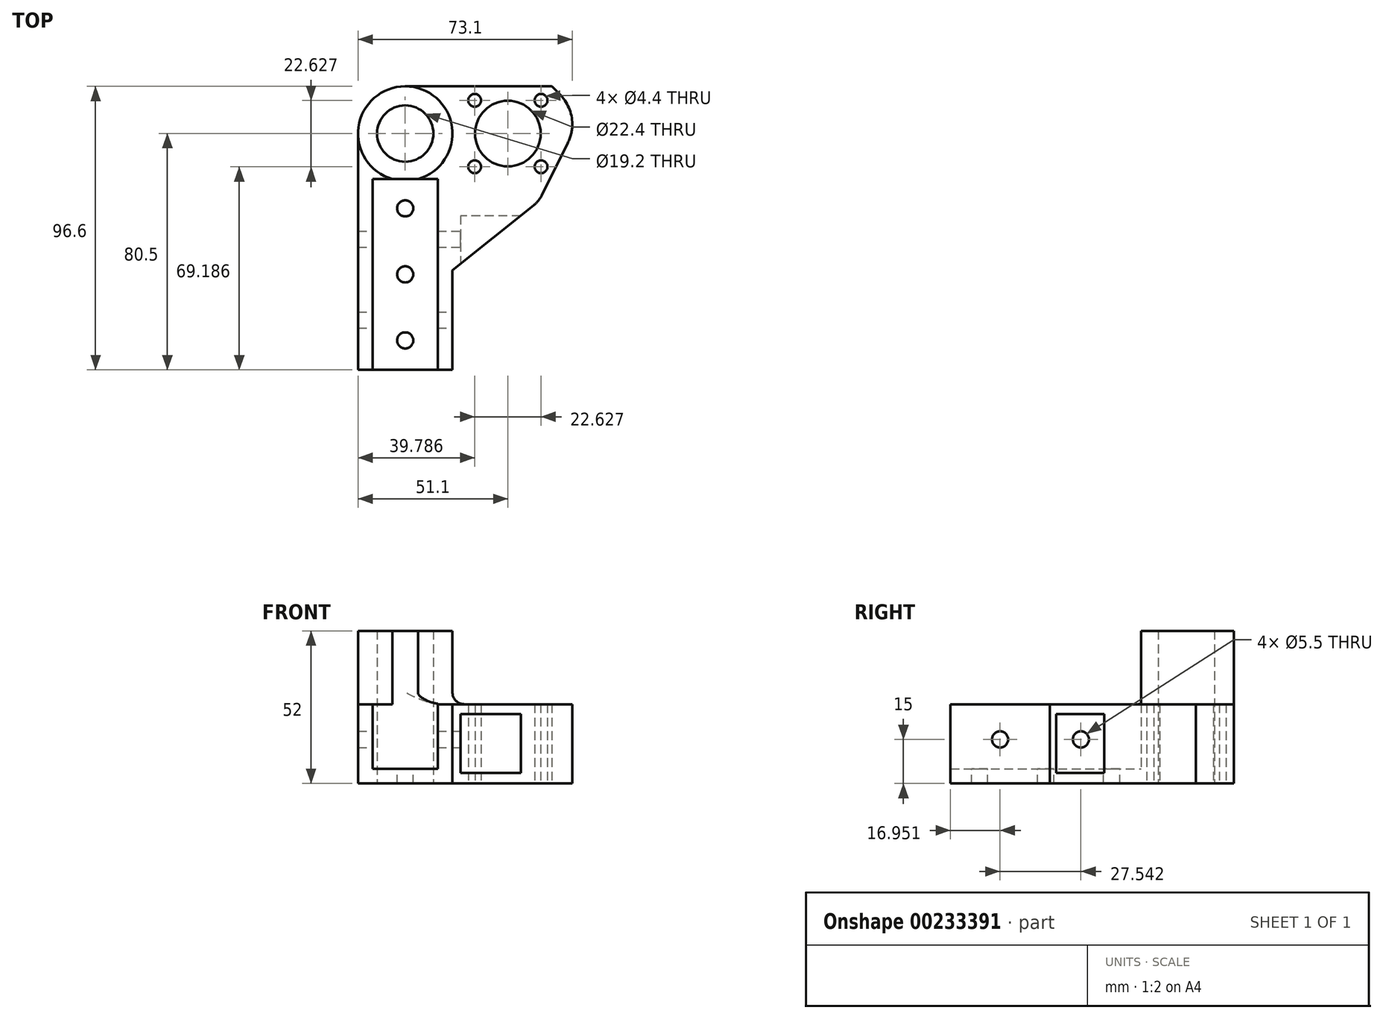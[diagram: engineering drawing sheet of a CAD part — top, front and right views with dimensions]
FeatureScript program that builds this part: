
annotation { "Feature Type Name" : "Feature", "Feature Type Description" : "" }
export const myFeature = defineFeature(function(context is Context, id is Id, definition is map)
    precondition{}
    {
        {
            var Q0;
            Q0=qCreatedBy(makeId("Top.planeOp"),FACE);
            var sketch = newSketch(context, id + "F0", { "sketchPlane" : qUnion([Q0])});
            skLineSegment(sketch, "E0.bottom", {"start": v(-10.1, -32.5) * mm, "end": v(10.1, -32.5) * mm, "construction": true});
            skLineSegment(sketch, "E0.top", {"start": v(-10.1, 32.5) * mm, "end": v(10.1, 32.5) * mm, "construction": true});
            skLineSegment(sketch, "E0.left", {"start": v(-10.1, -32.5) * mm, "end": v(-10.1, 32.5) * mm, "construction": true});
            skLineSegment(sketch, "E0.right", {"start": v(10.1, -32.5) * mm, "end": v(10.1, 32.5) * mm, "construction": true});
            skPoint(sketch, "E0.middle", {"position": v(0, 0) * mm});
            skLineSegment(sketch, "E1.bottom", {"start": v(-16.1, -32.5) * mm, "end": v(16.1, -32.5) * mm});
            skLineSegment(sketch, "E1.top", {"start": v(-16.1, 32.5) * mm, "end": v(16.1, 32.5) * mm});
            skLineSegment(sketch, "E1.left", {"start": v(-16.1, -32.5) * mm, "end": v(-16.1, 32.5) * mm});
            skLineSegment(sketch, "E1.right", {"start": v(16.1, -32.5) * mm, "end": v(16.1, 32.5) * mm});
            skCircle(sketch, "E2", {"center": v(0, 48) * mm, "radius": 9.6 * mm});
            skLineSegment(sketch, "E3", {"start": v(-16.1, 32.5) * mm, "end": v(-16.1, 48) * mm});
            skLineSegment(sketch, "E4", {"start": v(16.1, 32.5) * mm, "end": v(16.1, 48) * mm});
            skArc(sketch, "E5", {"start": v(16.1, 48) * mm, "mid": v(0, 64.1) * mm, "end": v(-16.1, 48) * mm});
            skCircle(sketch, "E6", {"center": v(35, 48) * mm, "radius": 11.2 * mm});
            skLineSegment(sketch, "E7", {"start": v(35, 48) * mm, "end": v(57, 48) * mm, "construction": true});
            skLineSegment(sketch, "E8", {"start": v(0, 64.1) * mm, "end": v(57, 64.1) * mm});
            skLineSegment(sketch, "E9", {"start": v(57, 64.1) * mm, "end": v(57, 48) * mm});
            skLineSegment(sketch, "E10", {"start": v(57, 48) * mm, "end": v(46.51, 26.9) * mm});
            skLineSegment(sketch, "E11", {"start": v(43.8, 23.53) * mm, "end": v(16.1, 1.4) * mm});
            skCircle(sketch, "E12", {"center": v(35, 48) * mm, "radius": 16 * mm, "construction": true});
            skLineSegment(sketch, "E13", {"start": v(35, 48) * mm, "end": v(46.31, 59.31) * mm, "construction": true});
            skCircle(sketch, "E14", {"center": v(46.31, 59.31) * mm, "radius": 2.2 * mm});
            skCircle(sketch, "E15.1.0", {"center": v(23.69, 59.31) * mm, "radius": 2.2 * mm});
            skCircle(sketch, "E15.2.0", {"center": v(23.69, 36.69) * mm, "radius": 2.2 * mm});
            skCircle(sketch, "E15.3.0", {"center": v(46.31, 36.69) * mm, "radius": 2.2 * mm});
            skPoint(sketch, "E16.visualSharp", {"position": v(45.53, 24.91) * mm});
            skArc(sketch, "E16.filletArc", {"start": v(43.8, 23.53) * mm, "mid": v(45.34, 25.06) * mm, "end": v(46.51, 26.9) * mm});
            skSolve(sketch);
        }
        {
            var Q0;
            Q0 = qSketchRegion(id + "F0", true);
            var Q1;
            {var subQ1=sQuery(id+"F0.wireOp",EDGE,"E1.bottom");Q1=makeQuery(id+"F0.imprint","IMPRINT",FACE,{"disambiguationData":[TD([[makeQuery(id+"F0.imprint","IMPRINT",EDGE,{"derivedFrom":subQ1}),1.0]])]});}
            extrude(context, id + "F1", {"entities" : qUnion([Q0, Q1]), "depth" : 5 * mm});
        }
        {
            var Q0;
            Q0=makeQuery(id+"F1.opExtrude","CAP_FACE",FACE,{"disambiguationData":[OSD([sQuery(id+"F0.wireOp",EDGE,"E1.bottom"),sQuery(id+"F0.wireOp",EDGE,"E1.left"),sQuery(id+"F0.wireOp",EDGE,"E1.right"),sQuery(id+"F0.wireOp",EDGE,"E2"),sQuery(id+"F0.wireOp",EDGE,"E3"),sQuery(id+"F0.wireOp",EDGE,"E5"),sQuery(id+"F0.wireOp",EDGE,"E6"),sQuery(id+"F0.wireOp",EDGE,"E8"),sQuery(id+"F0.wireOp",EDGE,"E9"),sQuery(id+"F0.wireOp",EDGE,"E10"),sQuery(id+"F0.wireOp",EDGE,"E11")])],"isStart":false});
            var sketch = newSketch(context, id + "F2", { "sketchPlane" : qUnion([Q0])});
            skLineSegment(sketch, "E17.bottom", {"start": v(-11.1, -32.5) * mm, "end": v(11.1, -32.5) * mm});
            skLineSegment(sketch, "E17.top", {"start": v(-11.1, 32.5) * mm, "end": v(11.1, 32.5) * mm});
            skLineSegment(sketch, "E17.left", {"start": v(-11.1, -32.5) * mm, "end": v(-11.1, 32.5) * mm});
            skLineSegment(sketch, "E17.right", {"start": v(11.1, -32.5) * mm, "end": v(11.1, 32.5) * mm});
            skPoint(sketch, "E17.middle", {"position": v(0, 0) * mm});
            skSolve(sketch);
        }
        {
            var Q0;
            Q0=makeQuery(id+"F2.imprint","IMPRINT",FACE,{"disambiguationData":[TD([[makeQuery(id+"F2.imprint","IMPRINT",EDGE,{"derivedFrom":sQuery(id+"F2.wireOp",EDGE,"E17.top")}),1.0]])]});
            extrude(context, id + "F3", {"entities" : qUnion([Q0]), "operationType" : NewBodyOperationType.ADD, "depth" : 22 * mm});
        }
        {
            var Q0;
            Q0=makeQuery(id+"F3.opExtrude","CAP_FACE",FACE,{"disambiguationData":[OSD([sQuery(id+"F0.wireOp",EDGE,"E1.bottom"),sQuery(id+"F0.wireOp",EDGE,"E1.left"),sQuery(id+"F0.wireOp",EDGE,"E1.right"),sQuery(id+"F0.wireOp",EDGE,"E2"),sQuery(id+"F0.wireOp",EDGE,"E3"),sQuery(id+"F0.wireOp",EDGE,"E5"),sQuery(id+"F0.wireOp",EDGE,"E6"),sQuery(id+"F0.wireOp",EDGE,"E8"),sQuery(id+"F0.wireOp",EDGE,"E9"),sQuery(id+"F0.wireOp",EDGE,"E10"),sQuery(id+"F0.wireOp",EDGE,"E11"),sQuery(id+"F0.wireOp",EDGE,"E14"),sQuery(id+"F0.wireOp",EDGE,"E15.1.0"),sQuery(id+"F0.wireOp",EDGE,"E15.2.0"),sQuery(id+"F0.wireOp",EDGE,"E15.3.0"),sQuery(id+"F0.wireOp",EDGE,"E16.filletArc"),sQuery(id+"F2.wireOp",EDGE,"E17.top"),sQuery(id+"F2.wireOp",EDGE,"E17.left"),sQuery(id+"F2.wireOp",EDGE,"E17.right")])],"isStart":false});
            var sketch = newSketch(context, id + "F4", { "sketchPlane" : qUnion([Q0])});
            skArc(sketch, "E18", {"start": v(23.58, 54.53) * mm, "mid": v(21.85, 48) * mm, "end": v(23.58, 41.47) * mm});
            skArc(sketch, "E19", {"start": v(28.47, 59.42) * mm, "mid": v(20.3, 62.7) * mm, "end": v(23.58, 54.53) * mm});
            skLineSegment(sketch, "E20", {"start": v(35, 34.85) * mm, "end": v(35, 61.15) * mm, "construction": true});
            skLineSegment(sketch, "E21", {"start": v(21.85, 48) * mm, "end": v(48.15, 48) * mm, "construction": true});
            skArc(sketch, "E22.MirrorC", {"start": v(41.53, 59.42) * mm, "mid": v(49.7, 62.7) * mm, "end": v(46.42, 54.53) * mm});
            skArc(sketch, "E23.trimOffspring", {"start": v(41.53, 59.42) * mm, "mid": v(35, 61.15) * mm, "end": v(28.47, 59.42) * mm});
            skArc(sketch, "E24.MirrorCS", {"start": v(28.47, 36.58) * mm, "mid": v(20.3, 33.3) * mm, "end": v(23.58, 41.47) * mm});
            skArc(sketch, "E25.MirrorCS", {"start": v(41.53, 36.58) * mm, "mid": v(49.7, 33.3) * mm, "end": v(46.42, 41.47) * mm});
            skArc(sketch, "E26.trimOffspring", {"start": v(28.47, 36.58) * mm, "mid": v(35, 34.85) * mm, "end": v(41.53, 36.58) * mm});
            skArc(sketch, "E27.trimOffspring", {"start": v(46.42, 41.47) * mm, "mid": v(48.15, 48) * mm, "end": v(46.42, 54.53) * mm});
            skCircle(sketch, "E28", {"center": v(0, 48) * mm, "radius": 16.1 * mm});
            skSolve(sketch);
        }
        {
            var Q0;
            Q0=makeQuery(id+"F4.imprint","IMPRINT",FACE,{"disambiguationData":[TD([[makeQuery(id+"F4.imprint","IMPRINT",EDGE,{"derivedFrom":makeQuery(id+"F3.opExtrude","CAP_EDGE",EDGE,{"disambiguationData":[OSD([sQuery(id+"F0.wireOp",EDGE,"E2")])],"isStart":false})}),-1.0]])]});
            extrude(context, id + "F5", {"entities" : qUnion([Q0]), "operationType" : NewBodyOperationType.ADD, "depth" : 25 * mm});
        }
        {
            var Q0;
            {var subQ1=sQuery(id+"F0.wireOp",EDGE,"E8");var subQ3=sQuery(id+"F4.wireOp",EDGE,"E28");Q0=makeQuery(id+"F5.boolean.opBoolean","SPLIT",EDGE,{"disambiguationData":[TD([makeQuery(id+"F1.opExtrude","SWEPT_FACE",FACE,{"disambiguationData":[OSD([subQ1])]})])],"derivedFrom":makeQuery(id+"F5.opExtrude","CAP_EDGE",EDGE,{"disambiguationData":[OSD([subQ3])],"isStart":true})});}
            var Q1;
            {var subQ2=sQuery(id+"F0.wireOp",EDGE,"E3");var subQ3=sQuery(id+"F0.wireOp",EDGE,"E1.left");var subQ4=sQuery(id+"F4.wireOp",EDGE,"E28");Q1=makeQuery(id+"F5.boolean.opBoolean","SPLIT",EDGE,{"disambiguationData":[TD([makeQuery(id+"F1.opExtrude","SWEPT_FACE",FACE,{"disambiguationData":[OSD([subQ3,subQ2])]})])],"derivedFrom":makeQuery(id+"F5.opExtrude","CAP_EDGE",EDGE,{"disambiguationData":[OSD([subQ4])],"isStart":true})});}
            fillet(context, id + "F6", {"entities" : qUnion([Q0, Q1]), "radius" : 4 * mm, "tangentPropagation" : true, "allowEdgeOverflow" : false});
        }
        {
            var Q0;
            Q0=qCreatedBy(makeId("Front.planeOp"),FACE);
            var sketch = newSketch(context, id + "F7", { "sketchPlane" : qUnion([Q0])});
            skLineSegment(sketch, "E29", {"start": v(18.86, 23.7) * mm, "end": v(18.86, 3.63) * mm});
            skLineSegment(sketch, "E30", {"start": v(18.86, 3.63) * mm, "end": v(40.79, 3.63) * mm});
            skLineSegment(sketch, "E31", {"start": v(40.79, 3.63) * mm, "end": v(40.79, 23.7) * mm});
            skLineSegment(sketch, "E32", {"start": v(40.79, 23.7) * mm, "end": v(18.86, 23.7) * mm});
            skSolve(sketch);
        }
        {
            var Q0;
            Q0=makeQuery(id+"F7.imprint","IMPRINT",FACE,{"disambiguationData":[TD([[makeQuery(id+"F7.imprint","IMPRINT",EDGE,{"derivedFrom":sQuery(id+"F7.wireOp",EDGE,"E29")}),1.0]])]});
            extrude(context, id + "F8", {"entities" : qUnion([Q0]), "operationType" : NewBodyOperationType.REMOVE, "oppositeDirection" : true, "depth" : 20 * mm});
        }
        {
            var Q0;
            Q0=makeQuery(id+"F1.opExtrude","CAP_FACE",FACE,{"disambiguationData":[OSD([sQuery(id+"F0.wireOp",EDGE,"E1.bottom"),sQuery(id+"F0.wireOp",EDGE,"E1.left"),sQuery(id+"F0.wireOp",EDGE,"E1.right"),sQuery(id+"F0.wireOp",EDGE,"E2"),sQuery(id+"F0.wireOp",EDGE,"E3"),sQuery(id+"F0.wireOp",EDGE,"E5"),sQuery(id+"F0.wireOp",EDGE,"E6"),sQuery(id+"F0.wireOp",EDGE,"E8"),sQuery(id+"F0.wireOp",EDGE,"E9"),sQuery(id+"F0.wireOp",EDGE,"E10"),sQuery(id+"F0.wireOp",EDGE,"E11"),sQuery(id+"F0.wireOp",EDGE,"E14"),sQuery(id+"F0.wireOp",EDGE,"E15.1.0"),sQuery(id+"F0.wireOp",EDGE,"E15.2.0"),sQuery(id+"F0.wireOp",EDGE,"E15.3.0"),sQuery(id+"F0.wireOp",EDGE,"E16.filletArc")])],"isStart":false});
            var sketch = newSketch(context, id + "F9", { "sketchPlane" : qUnion([Q0])});
            skLineSegment(sketch, "E33", {"start": v(0, -32.5) * mm, "end": v(0, 32.5) * mm, "construction": true});
            skCircle(sketch, "E34", {"center": v(0, 0) * mm, "radius": 2.75 * mm});
            skCircle(sketch, "E35", {"center": v(0, -22.5) * mm, "radius": 2.75 * mm});
            skCircle(sketch, "E36", {"center": v(0, 22.5) * mm, "radius": 2.75 * mm});
            skSolve(sketch);
        }
        {
            var Q0;
            Q0=makeQuery(id+"F9.imprint","IMPRINT",FACE,{"disambiguationData":[TD([[makeQuery(id+"F9.imprint","IMPRINT",EDGE,{"derivedFrom":sQuery(id+"F9.wireOp",EDGE,"E36")}),1.0]])]});
            var Q1;
            Q1=makeQuery(id+"F9.imprint","IMPRINT",FACE,{"disambiguationData":[TD([[makeQuery(id+"F9.imprint","IMPRINT",EDGE,{"derivedFrom":sQuery(id+"F9.wireOp",EDGE,"E34")}),1.0]])]});
            var Q2;
            Q2=makeQuery(id+"F9.imprint","IMPRINT",FACE,{"disambiguationData":[TD([[makeQuery(id+"F9.imprint","IMPRINT",EDGE,{"derivedFrom":sQuery(id+"F9.wireOp",EDGE,"E35")}),1.0]])]});
            extrude(context, id + "F10", {"entities" : qUnion([Q0, Q1, Q2]), "operationType" : NewBodyOperationType.REMOVE, "oppositeDirection" : true, "depth" : 25 * mm});
        }
        {
            var Q0;
            {var subQ0=sQuery(id+"F0.wireOp",EDGE,"E1.right");Q0=makeQuery(id+"F3.boolean.opBoolean","MERGE",FACE,{"derivedFrom":[makeQuery(id+"F1.opExtrude","SWEPT_FACE",FACE,{"disambiguationData":[OSD([subQ0])]}),makeQuery(id+"F3.opExtrude","SWEPT_FACE",FACE,{"disambiguationData":[OSD([subQ0])]})]});}
            var sketch = newSketch(context, id + "F11", { "sketchPlane" : qUnion([Q0])});
            skLineSegment(sketch, "E37", {"start": v(-15.55, 0) * mm, "end": v(-15.55, 15) * mm, "construction": true});
            skCircle(sketch, "E38", {"center": v(-15.55, 15) * mm, "radius": 2.75 * mm});
            skSolve(sketch);
        }
        {
            var Q0;
            Q0=makeQuery(id+"F8.boolean.opBoolean","COPY",FACE,{"derivedFrom":makeQuery(id+"F8.opExtrude","SWEPT_FACE",FACE,{"disambiguationData":[OSD([sQuery(id+"F7.wireOp",EDGE,"E29")])]})});
            var sketch = newSketch(context, id + "F12", { "sketchPlane" : qUnion([Q0])});
            skLineSegment(sketch, "E39", {"start": v(0, 0) * mm, "end": v(0, 15) * mm, "construction": true});
            skCircle(sketch, "E40", {"center": v(12, 15) * mm, "radius": 2.75 * mm});
            skSolve(sketch);
        }
        {
            var Q0;
            Q0=makeQuery(id+"F11.imprint","IMPRINT",FACE,{"disambiguationData":[TD([[makeQuery(id+"F11.imprint","IMPRINT",EDGE,{"derivedFrom":sQuery(id+"F11.wireOp",EDGE,"E38")}),1.0]])]});
            var Q1;
            Q1=makeQuery(id+"F12.imprint","IMPRINT",FACE,{"disambiguationData":[TD([[makeQuery(id+"F12.imprint","IMPRINT",EDGE,{"derivedFrom":sQuery(id+"F12.wireOp",EDGE,"E40")}),1.0]])]});
            extrude(context, id + "F13", {"entities" : qUnion([Q0, Q1]), "operationType" : NewBodyOperationType.REMOVE, "oppositeDirection" : true, "depth" : 50 * mm});
        }
        {
            var Q0;
            {var subQ0=sQuery(id+"F0.wireOp",EDGE,"E9");var subQ1=sQuery(id+"F0.wireOp",EDGE,"E8");Q0=makeQuery(id+"F3.boolean.opBoolean","MERGE",EDGE,{"derivedFrom":[makeQuery(id+"F1.opExtrude","SWEPT_EDGE",EDGE,{"disambiguationData":[OSD([subQ1,subQ0])]}),makeQuery(id+"F3.opExtrude","SWEPT_EDGE",EDGE,{"disambiguationData":[OSD([subQ1,subQ0])]})]});}
            chamfer(context, id + "F14", {"entities" : qUnion([Q0]), "width" : 7 * mm, "tangentPropagation" : true});
        }
        {
            var Q0;
            {var subQ0=sQuery(id+"F0.wireOp",EDGE,"E9");var subQ1=sQuery(id+"F0.wireOp",EDGE,"E8");Q0=makeQuery(id+"F14.opChamfer","BLEND_EDGE",EDGE,{"blendedFrom":[makeQuery(id+"F3.boolean.opBoolean","MERGE",EDGE,{"derivedFrom":[makeQuery(id+"F1.opExtrude","SWEPT_EDGE",EDGE,{"disambiguationData":[OSD([subQ1,subQ0])]}),makeQuery(id+"F3.opExtrude","SWEPT_EDGE",EDGE,{"disambiguationData":[OSD([subQ1,subQ0])]})]}),makeQuery(id+"F3.boolean.opBoolean","MERGE",FACE,{"derivedFrom":[makeQuery(id+"F1.opExtrude","SWEPT_FACE",FACE,{"disambiguationData":[OSD([subQ0])]}),makeQuery(id+"F3.opExtrude","SWEPT_FACE",FACE,{"disambiguationData":[OSD([subQ0])]})]})],"blendedInto":[makeQuery(id+"F3.boolean.opBoolean","MERGE",FACE,{"derivedFrom":[makeQuery(id+"F1.opExtrude","SWEPT_FACE",FACE,{"disambiguationData":[OSD([subQ0])]}),makeQuery(id+"F3.opExtrude","SWEPT_FACE",FACE,{"disambiguationData":[OSD([subQ0])]})]})]});}
            var Q1;
            {var subQ0=sQuery(id+"F0.wireOp",EDGE,"E10");var subQ1=sQuery(id+"F0.wireOp",EDGE,"E9");Q1=makeQuery(id+"F3.boolean.opBoolean","MERGE",EDGE,{"derivedFrom":[makeQuery(id+"F1.opExtrude","SWEPT_EDGE",EDGE,{"disambiguationData":[OSD([subQ1,subQ0])]}),makeQuery(id+"F3.opExtrude","SWEPT_EDGE",EDGE,{"disambiguationData":[OSD([subQ1,subQ0])]})]});}
            fillet(context, id + "F15", {"entities" : qUnion([Q0, Q1]), "radius" : 15 * mm, "tangentPropagation" : true, "allowEdgeOverflow" : false});
        }
    });
